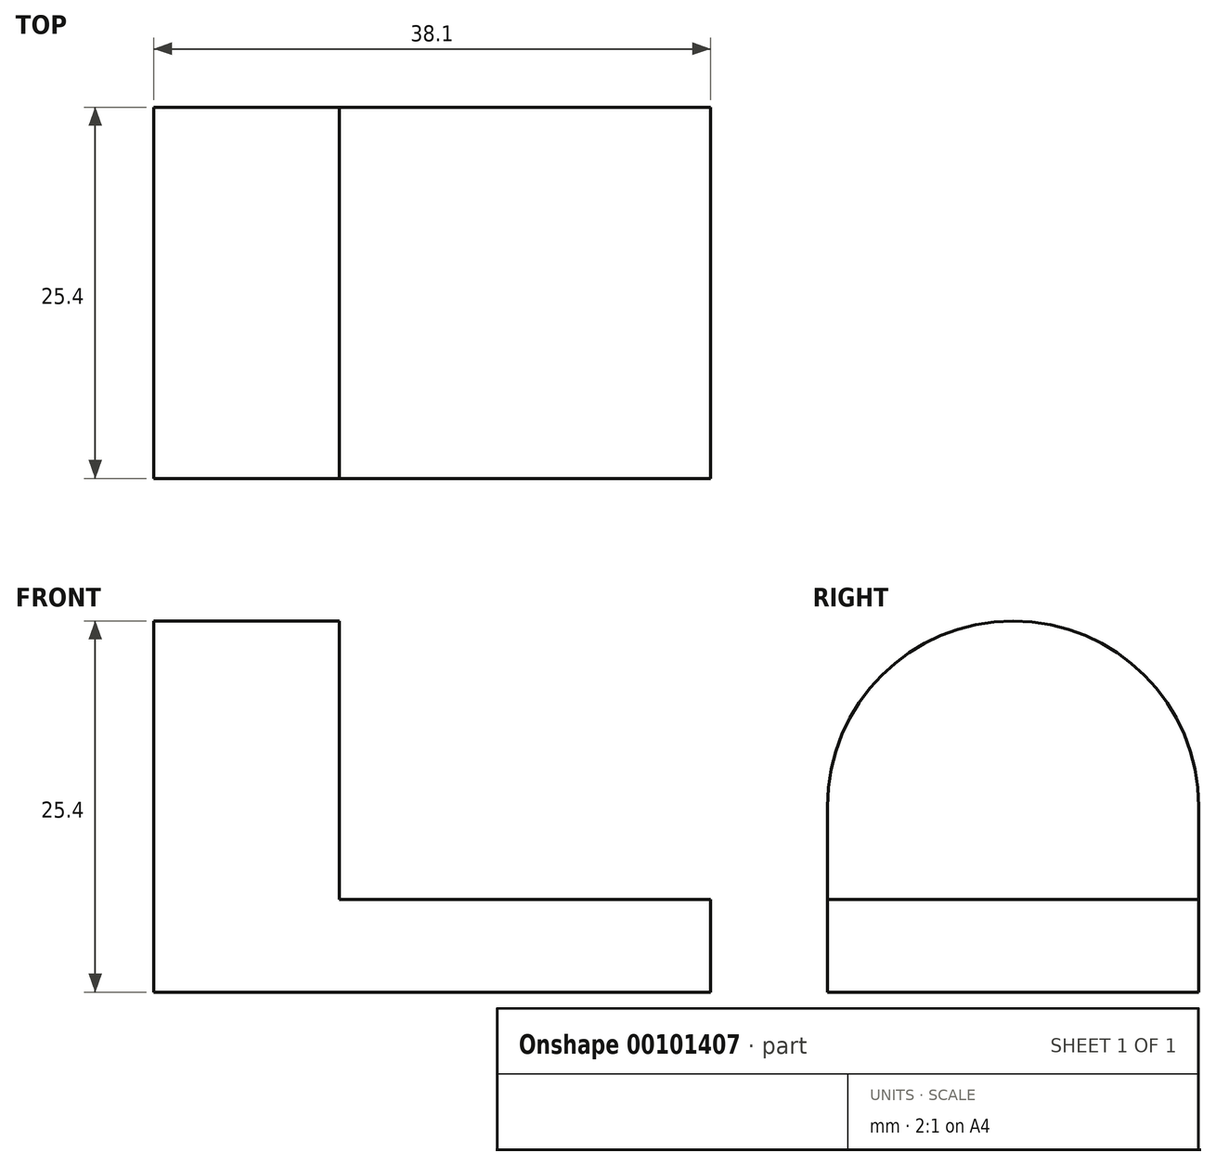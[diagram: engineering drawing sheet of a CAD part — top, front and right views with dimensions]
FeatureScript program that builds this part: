
annotation { "Feature Type Name" : "Feature", "Feature Type Description" : "" }
export const myFeature = defineFeature(function(context is Context, id is Id, definition is map)
    precondition{}
    {
        {
            var Q0;
            Q0=qCreatedBy(makeId("Front.planeOp"),FACE);
            var sketch = newSketch(context, id + "F0", { "sketchPlane" : qUnion([Q0])});
            skLineSegment(sketch, "E0", {"start": v(0, 0) * mm, "end": v(38.1, 0) * mm});
            skLineSegment(sketch, "E1", {"start": v(38.1, 0) * mm, "end": v(38.1, 6.35) * mm});
            skLineSegment(sketch, "E2", {"start": v(38.1, 6.35) * mm, "end": v(0, 6.35) * mm});
            skLineSegment(sketch, "E3", {"start": v(0, 6.35) * mm, "end": v(0, 0) * mm});
            skSolve(sketch);
        }
        {
            var Q0;
            Q0 = qSketchRegion(id + "F0", true);
            extrude(context, id + "F1", {"entities" : qUnion([Q0]), "depth" : 25.4 * mm});
        }
        {
            var Q0;
            Q0=makeQuery(id+"F1.opExtrude","SWEPT_FACE",FACE,{"disambiguationData":[OSD([sQuery(id+"F0.wireOp",EDGE,"E3")])]});
            var sketch = newSketch(context, id + "F2", { "sketchPlane" : qUnion([Q0])});
            skLineSegment(sketch, "E4", {"start": v(25.4, 6.35) * mm, "end": v(25.4, 12.7) * mm});
            skLineSegment(sketch, "E5", {"start": v(0, 6.35) * mm, "end": v(0, 12.7) * mm});
            skArc(sketch, "E6", {"start": v(25.4, 12.7) * mm, "mid": v(12.7, 25.4) * mm, "end": v(0, 12.7) * mm});
            skSolve(sketch);
        }
        {
            var Q0;
            Q0=makeQuery(id+"F2.imprint","IMPRINT",FACE,{"disambiguationData":[TD([[makeQuery(id+"F2.imprint","IMPRINT",EDGE,{"derivedFrom":sQuery(id+"F2.wireOp",EDGE,"E4")}),1.0]])]});
            var Q1;
            Q1 = qSketchRegion(id + "F2", true);
            extrude(context, id + "F3", {"entities" : qUnion([Q0, Q1]), "operationType" : NewBodyOperationType.ADD, "oppositeDirection" : true, "depth" : 12.7 * mm});
        }
    });
